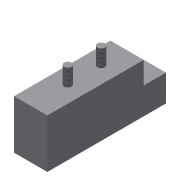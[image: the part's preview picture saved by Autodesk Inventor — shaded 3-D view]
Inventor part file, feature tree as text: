
AUTODESK INVENTOR PART (.ipt)
format: ipt  version: 2016 SP2 (Build 200236200, 236)  size: 107,520 bytes
history: native  units: mm
features: extrude x3, sketch x3, thread x2, projected_geometry x1
ambient origin geometry x8: Origin, YZ Plane, XZ Plane, XY Plane, X Axis, Y Axis, Z Axis, Center Point
bodies: Body1 (feature_tree)
feature tree (9):
  extrude  "Extrusion3"  Depth=45.0mm
  extrude  "Extrusion4"  Depth=10.0mm
  thread  "Thread1"  [1 undecoded]
  thread  "Thread2"  [1 undecoded]
  extrude  "Extrusion5"  Depth=10.0mm TaperAngle=0.0deg
  sketch  "Sketch1"  dims[d4=160.0mm d5=45.0mm]
  sketch  "Sketch2"  dims[d6=66.0mm d7=0.0mm d8=10.0mm d9=50.0mm d10=45.0mm]
  sketch  "Sketch3"  dims[d11=23.0mm d12=0.0mm d13=10.0mm d14=0.0mm d15=10.0mm d16=0.0mm d17=30.0mm d18=30.0mm d19=10.0mm d20=0.0mm]
  projected_geometry  "Projected Loop1"
note: 2 required parameter values undecoded (feature->parameter linkage not recoverable at this tier; creation-order binding heuristic only, values carry confidence <= 0.55)
